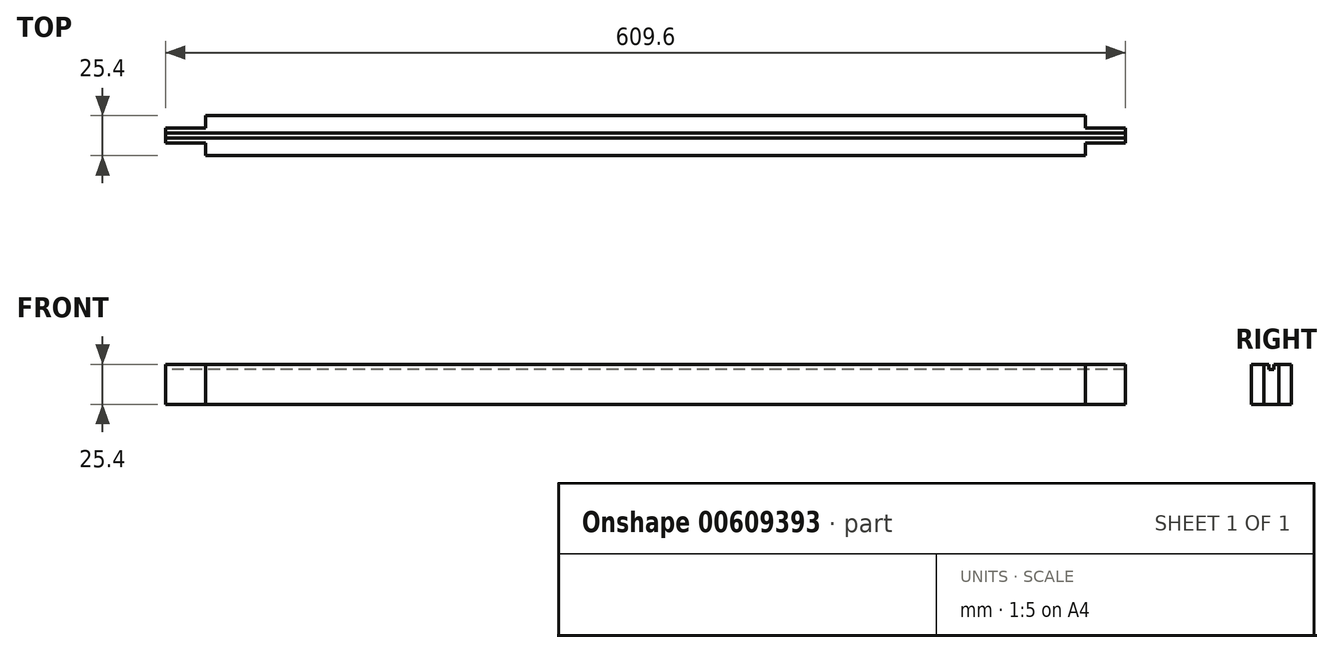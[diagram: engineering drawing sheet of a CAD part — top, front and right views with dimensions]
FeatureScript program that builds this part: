
annotation { "Feature Type Name" : "Feature", "Feature Type Description" : "" }
export const myFeature = defineFeature(function(context is Context, id is Id, definition is map)
    precondition{}
    {
        {
            var Q0;
            Q0=qCreatedBy(makeId("Front.planeOp"),FACE);
            var sketch = newSketch(context, id + "F0", { "sketchPlane" : qUnion([Q0])});
            skLineSegment(sketch, "E0.bottom", {"start": v(279.4, 12.7) * mm, "end": v(-279.4, 12.7) * mm});
            skLineSegment(sketch, "E0.top", {"start": v(279.4, -12.7) * mm, "end": v(-279.4, -12.7) * mm});
            skLineSegment(sketch, "E0.left", {"start": v(279.4, 12.7) * mm, "end": v(279.4, -12.7) * mm});
            skLineSegment(sketch, "E0.right", {"start": v(-279.4, 12.7) * mm, "end": v(-279.4, -12.7) * mm});
            skPoint(sketch, "E0.middle", {"position": v(0, 0) * mm});
            skSolve(sketch);
        }
        {
            var Q0;
            Q0=makeQuery(id+"F0.imprint","IMPRINT",FACE,{"disambiguationData":[TD([[makeQuery(id+"F0.imprint","IMPRINT",EDGE,{"derivedFrom":sQuery(id+"F0.wireOp",EDGE,"E0.bottom")}),1.0]])]});
            extrude(context, id + "F1", {"entities" : qUnion([Q0]), "depth" : 25.4 * mm, "offsetDistance" : 25.4 * mm});
        }
        {
            var Q0;
            Q0=makeQuery(id+"F1.opExtrude","SWEPT_FACE",FACE,{"disambiguationData":[OSD([sQuery(id+"F0.wireOp",EDGE,"E0.bottom")])]});
            var sketch = newSketch(context, id + "F2", { "sketchPlane" : qUnion([Q0])});
            skLineSegment(sketch, "E1.bottom", {"start": v(990.6, -11.11) * mm, "end": v(-1549.4, -11.11) * mm});
            skLineSegment(sketch, "E1.top", {"start": v(990.6, -14.29) * mm, "end": v(-1549.4, -14.29) * mm});
            skLineSegment(sketch, "E1.left", {"start": v(990.6, -11.11) * mm, "end": v(990.6, -14.29) * mm});
            skLineSegment(sketch, "E1.right", {"start": v(-1549.4, -11.11) * mm, "end": v(-1549.4, -14.29) * mm});
            skPoint(sketch, "E1.middle", {"position": v(-279.4, -12.7) * mm});
            skSolve(sketch);
        }
        {
            var Q0;
            {var subQ0=sQuery(id+"F2.wireOp",EDGE,"E1.bottom");var subQ1=sQuery(id+"F0.wireOp",EDGE,"E0.bottom");var subQ2=makeQuery(id+"F1.opExtrude","SWEPT_EDGE",EDGE,{"disambiguationData":[OSD([subQ1,sQuery(id+"F0.wireOp",EDGE,"E0.left")])]});var subQ3=makeQuery(id+"F2.imprint","INTERSECT",VERTEX,{"derivedFrom":[subQ2,subQ0]});Q0=makeQuery(id+"F2.imprint","IMPRINT",FACE,{"disambiguationData":[TD([[makeQuery(id+"F2.imprint","IMPRINT",EDGE,{"disambiguationData":[TD([[subQ3,-1.0]])],"derivedFrom":subQ0}),1.0]])]});}
            extrude(context, id + "F3", {"entities" : qUnion([Q0]), "operationType" : NewBodyOperationType.REMOVE, "oppositeDirection" : true, "depth" : 3.17 * mm, "offsetDistance" : 25.4 * mm});
        }
        {
            var Q0;
            Q0=makeQuery(id+"F1.opExtrude","SWEPT_FACE",FACE,{"disambiguationData":[OSD([sQuery(id+"F0.wireOp",EDGE,"E0.right")])]});
            var sketch = newSketch(context, id + "F4", { "sketchPlane" : qUnion([Q0])});
            skLineSegment(sketch, "E2.bottom", {"start": v(25.4, -12.7) * mm, "end": v(17.46, -12.7) * mm});
            skLineSegment(sketch, "E2.top", {"start": v(25.4, 12.7) * mm, "end": v(17.46, 12.7) * mm});
            skLineSegment(sketch, "E2.left", {"start": v(25.4, -12.7) * mm, "end": v(25.4, 12.7) * mm});
            skLineSegment(sketch, "E2.right", {"start": v(17.46, -12.7) * mm, "end": v(17.46, 12.7) * mm});
            skLineSegment(sketch, "E3.bottom", {"start": v(17.46, -12.7) * mm, "end": v(7.94, -12.7) * mm});
            skLineSegment(sketch, "E3.top", {"start": v(17.46, 12.7) * mm, "end": v(7.94, 12.7) * mm});
            skLineSegment(sketch, "E3.right", {"start": v(7.94, -12.7) * mm, "end": v(7.94, 12.7) * mm});
            skSolve(sketch);
        }
        {
            var Q0;
            Q0=makeQuery(id+"F4.imprint","IMPRINT",FACE,{"disambiguationData":[TD([[makeQuery(id+"F4.imprint","IMPRINT",EDGE,{"derivedFrom":sQuery(id+"F4.wireOp",EDGE,"E3.bottom")}),-1.0]])]});
            extrude(context, id + "F5", {"entities" : qUnion([Q0]), "operationType" : NewBodyOperationType.ADD, "depth" : 25.4 * mm, "offsetDistance" : 25.4 * mm});
        }
        {
            var Q0;
            Q0=makeQuery(id+"F1.opExtrude","SWEPT_FACE",FACE,{"disambiguationData":[OSD([sQuery(id+"F0.wireOp",EDGE,"E0.left")])]});
            var sketch = newSketch(context, id + "F6", { "sketchPlane" : qUnion([Q0])});
            skLineSegment(sketch, "E4.bottom", {"start": v(0, -12.7) * mm, "end": v(-7.94, -12.7) * mm});
            skLineSegment(sketch, "E4.top", {"start": v(0, 12.7) * mm, "end": v(-7.94, 12.7) * mm});
            skLineSegment(sketch, "E4.left", {"start": v(0, -12.7) * mm, "end": v(0, 12.7) * mm});
            skLineSegment(sketch, "E4.right", {"start": v(-7.94, -12.7) * mm, "end": v(-7.94, 12.7) * mm});
            skLineSegment(sketch, "E5.bottom", {"start": v(-7.94, -12.7) * mm, "end": v(-17.46, -12.7) * mm});
            skLineSegment(sketch, "E5.top", {"start": v(-7.94, 12.7) * mm, "end": v(-17.46, 12.7) * mm});
            skLineSegment(sketch, "E5.right", {"start": v(-17.46, -12.7) * mm, "end": v(-17.46, 12.7) * mm});
            skSolve(sketch);
        }
        {
            var Q0;
            Q0=makeQuery(id+"F6.imprint","IMPRINT",FACE,{"disambiguationData":[TD([[makeQuery(id+"F6.imprint","IMPRINT",EDGE,{"derivedFrom":sQuery(id+"F6.wireOp",EDGE,"E5.bottom")}),1.0]])]});
            extrude(context, id + "F7", {"entities" : qUnion([Q0]), "operationType" : NewBodyOperationType.ADD, "depth" : 25.4 * mm, "offsetDistance" : 25.4 * mm});
        }
    });
